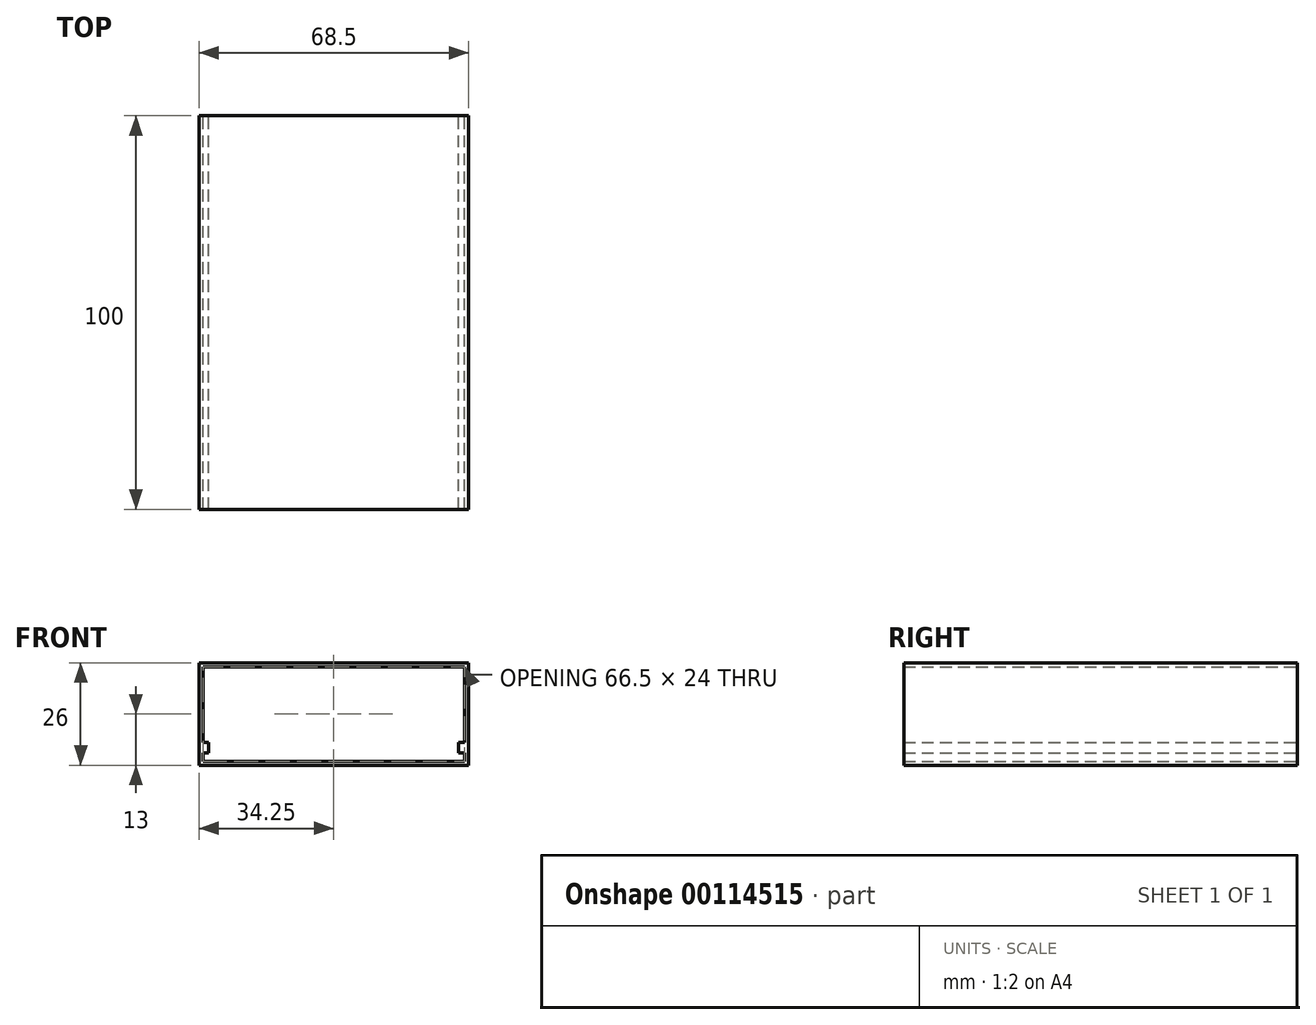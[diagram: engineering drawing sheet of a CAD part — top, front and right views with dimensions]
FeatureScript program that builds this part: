
annotation { "Feature Type Name" : "Feature", "Feature Type Description" : "" }
export const myFeature = defineFeature(function(context is Context, id is Id, definition is map)
    precondition{}
    {
        {
            var Q0;
            Q0=qCreatedBy(makeId("Front.planeOp"),FACE);
            var sketch = newSketch(context, id + "F0", { "sketchPlane" : qUnion([Q0])});
            skLineSegment(sketch, "E0.bottom", {"start": v(0, 13) * mm, "end": v(34.25, 13) * mm});
            skLineSegment(sketch, "E0.top", {"start": v(0, -13) * mm, "end": v(34.25, -13) * mm});
            skLineSegment(sketch, "E0.right", {"start": v(34.25, 13) * mm, "end": v(34.25, -13) * mm});
            skPoint(sketch, "E0.middle", {"position": v(0, 0) * mm});
            skLineSegment(sketch, "E1.top", {"start": v(0, -12) * mm, "end": v(33.25, -12) * mm});
            skLineSegment(sketch, "E2", {"start": v(33.25, -12) * mm, "end": v(0, -12) * mm});
            skLineSegment(sketch, "E3", {"start": v(33.25, -9.85) * mm, "end": v(33.25, -12) * mm});
            skLineSegment(sketch, "E4", {"start": v(31.75, -9.85) * mm, "end": v(33.25, -9.85) * mm});
            skLineSegment(sketch, "E5", {"start": v(31.75, -7.28) * mm, "end": v(31.75, -9.85) * mm});
            skLineSegment(sketch, "E6", {"start": v(31.75, -7.28) * mm, "end": v(33.25, -7.28) * mm});
            skLineSegment(sketch, "E7", {"start": v(0, 13) * mm, "end": v(0, 12) * mm});
            skLineSegment(sketch, "E8", {"start": v(33.25, -7.28) * mm, "end": v(33.25, 12) * mm});
            skLineSegment(sketch, "E9", {"start": v(33.25, 12) * mm, "end": v(0, 12) * mm});
            skLineSegment(sketch, "E10.trimOffspring", {"start": v(0, -12) * mm, "end": v(0, -13) * mm});
            skSolve(sketch);
        }
        {
            var Q0;
            Q0=makeQuery(id+"F0.imprint","IMPRINT",FACE,{"disambiguationData":[TD([[makeQuery(id+"F0.imprint","IMPRINT",EDGE,{"derivedFrom":sQuery(id+"F0.wireOp",EDGE,"E0.bottom")}),-1.0]])]});
            extrude(context, id + "F1", {"entities" : qUnion([Q0]), "depth" : 100 * mm});
        }
        {
            var Q0;
            Q0=makeQuery(id+"F1.opExtrude","SWEPT_BODY",BODY,{"disambiguationData":[OSD([sQuery(id+"F0.wireOp",EDGE,"E0.bottom"),sQuery(id+"F0.wireOp",EDGE,"E0.top"),sQuery(id+"F0.wireOp",EDGE,"E0.right"),sQuery(id+"F0.wireOp",EDGE,"E2"),sQuery(id+"F0.wireOp",EDGE,"E3"),sQuery(id+"F0.wireOp",EDGE,"E4"),sQuery(id+"F0.wireOp",EDGE,"E5"),sQuery(id+"F0.wireOp",EDGE,"E6"),sQuery(id+"F0.wireOp",EDGE,"E7"),sQuery(id+"F0.wireOp",EDGE,"E8"),sQuery(id+"F0.wireOp",EDGE,"E9")])]});
            var Q1;
            {var subQ0=sQuery(id+"F0.wireOp",EDGE,"E7");Q1=makeQuery(id+"F1.opExtrude","SWEPT_FACE",FACE,{"disambiguationData":[OSD([subQ0]),TDD([makeQuery(id+"F0.imprint","IMPRINT",EDGE,{"disambiguationData":[TD([[makeQuery(id+"F0.imprint","INTERSECT",VERTEX,{"derivedFrom":[sQuery(id+"F0.wireOp",EDGE,"E0.bottom"),subQ0]}),-1.0]])],"derivedFrom":subQ0})])]});}
            mirror(context, id + "F2", {"operationType" : NewBodyOperationType.ADD, "entities" : qUnion([Q0]), "mirrorPlane" : qUnion([Q1])});
        }
    });
